# Revit family: РИДАН_Кран шаровой_RJIP Premium FF WG_PN16_DN65-300
name_source: partatom
category: Арматура трубопроводов
units: mm (PartAtom-declared; Revit-internal decimal feet)

## family parameters
Всегда вертикально = Да
На основе рабочей плоскости = Нет
Общий = Нет
При загрузке вырезать с полостями = Нет
Размер круглого соединителя = Использовать диаметр
Тип детали = Вставляется

## types (8) — shared parameters
ADSK_Версия Revit = 2019
ADSK_Версия семейства = 1.0
ADSK_Единица измерения = шт.
ADSK_Завод-изготовитель = ООО «Ридан-Трейд»
ADSK_Количество = 1
ADSK_Материал = <По категории>
ADSK_Потеря давления жидкости = 0.0 Па
ADSK_Расход жидкости = 0.0000 м³/ч
LT = R-JIP_PN16
URL = https://ridan.ru

## per-type parameters (varying)
- DN65: ADSK_Диаметр условный=65 мм; ADSK_Код изделия=065N0331R; ADSK_Марка=RJIP Premium FF WG PN25 DN65; ADSK_Масса=13; ADSK_Наименование=Кран шаровой RJIP Premium фланцевый с ручным редукторным приводом PN25, Tmax=180C, DN65; ADSK_Пропускная способность=160.0000 м³/ч; a=180 мм; b=128 мм; c=122 мм; d=76 мм; d1=38 мм; e=3 мм; f=21 мм; g=61 мм; h=120 мм; i=60 мм; j=59 мм; k=114 мм; k1=57 мм; l=93 мм; m=8 мм; n=90 мм; o=34 мм; p=10 мм; q=10 мм; r=10 мм; НЧ=Нет; Редуктор_125_150=Нет; Редуктор_200=Нет; Редуктор_250_300=Нет; Редуктор_65=Да; Редуктор_80_100=Нет; УГО_Длина=290 мм
- DN80: ADSK_Диаметр условный=80 мм; ADSK_Код изделия=065N0336R; ADSK_Марка=RJIP Premium FF WG PN25 DN80; ADSK_Масса=18; ADSK_Наименование=Кран шаровой RJIP Premium фланцевый с ручным редукторным приводом PN25, Tmax=180C, DN80; ADSK_Пропускная способность=280.0000 м³/ч; a=195 мм; b=139 мм; c=133 мм; d=89 мм; d1=45 мм; e=3 мм; f=23 мм; g=54 мм; h=150 мм; i=75 мм; j=80 мм; k=140 мм; k1=70 мм; l=110 мм; m=8 мм; n=90 мм; o=39 мм; p=10 мм; q=10 мм; r=10 мм; НЧ=Нет; Редуктор_125_150=Нет; Редуктор_200=Нет; Редуктор_250_300=Нет; Редуктор_65=Нет; Редуктор_80_100=Да; УГО_Длина=310 мм
- DN100: ADSK_Диаметр условный=100 мм; ADSK_Код изделия=065N0241R; ADSK_Марка=RJIP Premium FF WG PN16 DN100; ADSK_Масса=26; ADSK_Наименование=Кран шаровой RJIP Premium фланцевый с ручным редукторным приводом PN16, Tmax=180C, DN100; ADSK_Пропускная способность=450.0000 м³/ч; a=230 мм; b=164 мм; c=158 мм; d=108 мм; d1=54 мм; e=3 мм; f=17 мм; g=50 мм; h=160 мм; i=80 мм; j=80 мм; k=159 мм; k1=80 мм; l=120 мм; m=10 мм; n=90 мм; o=39 мм; p=10 мм; q=10 мм; r=10 мм; НЧ=Нет; Редуктор_125_150=Нет; Редуктор_200=Нет; Редуктор_250_300=Нет; Редуктор_65=Нет; Редуктор_80_100=Да; УГО_Длина=300 мм
- DN125: ADSK_Диаметр условный=125 мм; ADSK_Код изделия=065N0246R; ADSK_Марка=RJIP Premium FF WG PN16 DN125; ADSK_Масса=37; ADSK_Наименование=Кран шаровой RJIP Premium фланцевый с ручным редукторным приводом PN16, Tmax=180C, DN125; ADSK_Пропускная способность=690.0000 м³/ч; a=270 мм; b=190 мм; c=184 мм; d=133 мм; d1=67 мм; e=3 мм; f=19 мм; g=49 мм; h=183 мм; i=92 мм; j=83 мм; k=180 мм; k1=90 мм; l=129 мм; m=13 мм; n=125 мм; o=49 мм; p=10 мм; q=10 мм; r=10 мм; НЧ=Нет; Редуктор_125_150=Да; Редуктор_200=Нет; Редуктор_250_300=Нет; Редуктор_65=Нет; Редуктор_80_100=Нет; УГО_Длина=325 мм
- DN150: ADSK_Диаметр условный=150 мм; ADSK_Код изделия=065N0251GR; ADSK_Марка=RJIP Premium FF WG PN16 DN150; ADSK_Масса=40; ADSK_Наименование=Кран шаровой RJIP Premium фланцевый с ручным редукторным приводом PN16, Tmax=180C, DN150; ADSK_Пропускная способность=1190.0000 м³/ч; a=300 мм; b=218 мм; c=212 мм; d=159 мм; d1=80 мм; e=3 мм; f=27 мм; g=35 мм; h=220 мм; i=110 мм; j=110 мм; k=219 мм; k1=110 мм; l=149 мм; m=13 мм; n=125 мм; o=49 мм; p=10 мм; q=10 мм; r=10 мм; НЧ=Нет; Редуктор_125_150=Да; Редуктор_200=Нет; Редуктор_250_300=Нет; Редуктор_65=Нет; Редуктор_80_100=Нет; УГО_Длина=350 мм
- DN200: ADSK_Диаметр условный=200 мм; ADSK_Код изделия=065N0256GR; ADSK_Марка=RJIP Premium FF WG PN16 DN200; ADSK_Масса=68; ADSK_Наименование=Кран шаровой RJIP Premium фланцевый с ручным редукторным приводом PN16, Tmax=180C, DN200; ADSK_Пропускная способность=1680.0000 м³/ч; a=360 мм; b=283 мм; c=278 мм; d=219 мм; d1=110 мм; e=3 мм; f=29 мм; g=18 мм; h=300 мм; i=150 мм; j=171 мм; k=273 мм; k1=137 мм; l=197 мм; m=18 мм; n=150 мм; o=78 мм; p=48 мм; q=48 мм; r=137 мм; НЧ=Да; Редуктор_125_150=Нет; Редуктор_200=Да; Редуктор_250_300=Нет; Редуктор_65=Нет; Редуктор_80_100=Нет; УГО_Длина=400 мм
- DN250: ADSK_Диаметр условный=250 мм; ADSK_Код изделия=065N0261GR; ADSK_Марка=RJIP Premium FF WG PN16 DN250; ADSK_Масса=124; ADSK_Наименование=Кран шаровой RJIP Premium фланцевый с ручным редукторным приводом PN16, Tmax=180C, DN250; ADSK_Пропускная способность=3210.0000 м³/ч; a=425 мм; b=341 мм; c=335 мм; d=273 мм; d1=137 мм; e=3 мм; f=31 мм; g=95 мм; h=392 мм; i=196 мм; j=230 мм; k=351 мм; k1=176 мм; l=236 мм; m=18 мм; n=210 мм; o=78 мм; p=48 мм; q=48 мм; r=176 мм; НЧ=Да; Редуктор_125_150=Нет; Редуктор_200=Нет; Редуктор_250_300=Да; Редуктор_65=Нет; Редуктор_80_100=Нет; УГО_Длина=650 мм
- DN300: ADSK_Диаметр условный=300 мм; ADSK_Код изделия=065N0266GR; ADSK_Марка=RJIP Premium FF WG PN16 DN300; ADSK_Масса=196; ADSK_Наименование=Кран шаровой RJIP Premium фланцевый с ручным редукторным приводом PN16, Tmax=180C, DN300; ADSK_Пропускная способность=4850.0000 м³/ч; a=550 мм; b=458 мм; c=450 мм; d=325 мм; d1=163 мм; e=4 мм; f=38 мм; g=63 мм; h=540 мм; i=267 мм; j=300 мм; k=450 мм; k1=225 мм; l=296 мм; m=18 мм; n=210 мм; o=88 мм; p=62 мм; q=58 мм; r=225 мм; НЧ=Да; Редуктор_125_150=Нет; Редуктор_200=Нет; Редуктор_250_300=Да; Редуктор_65=Нет; Редуктор_80_100=Нет; УГО_Длина=750 мм
